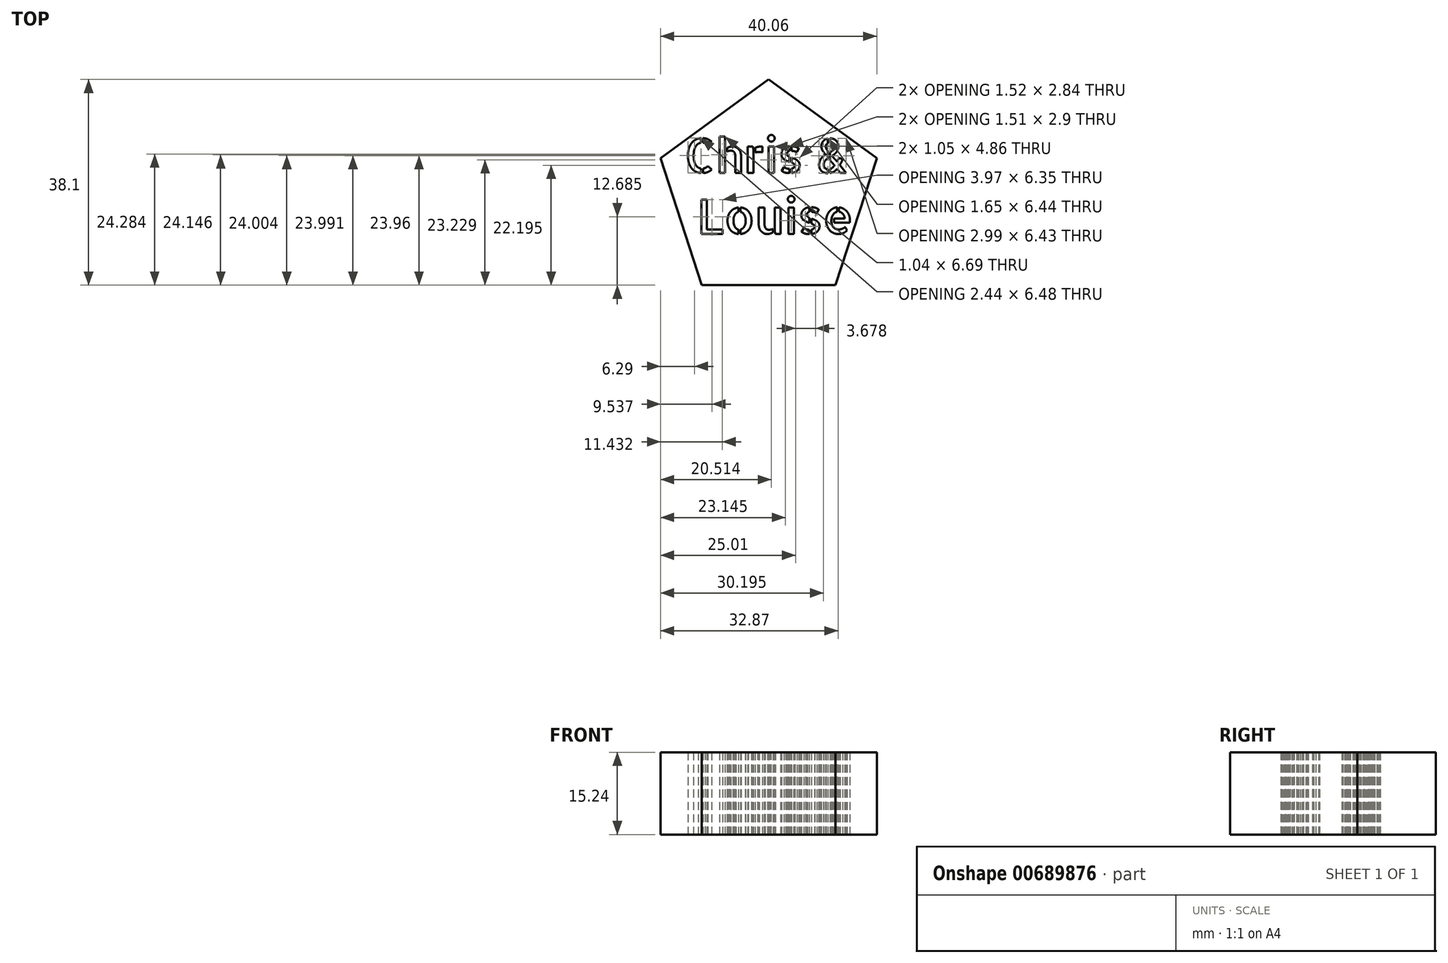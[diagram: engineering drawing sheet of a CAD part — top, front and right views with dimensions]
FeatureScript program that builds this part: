
annotation { "Feature Type Name" : "Feature", "Feature Type Description" : "" }
export const myFeature = defineFeature(function(context is Context, id is Id, definition is map)
    precondition{}
    {
        {
            var Q0;
            Q0=qCreatedBy(makeId("Top.planeOp"),FACE);
            var sketch = newSketch(context, id + "F0", { "sketchPlane" : qUnion([Q0])});
            skText(sketch, "E0", { "text": "Chris &\n Louise", "fontName": "AllertaStencil-Regular.ttf"});
            skCircle(sketch, "E1.cCircle", {"center": v(0, 0) * mm, "radius": 17.04 * mm, "construction": true});
            skLineSegment(sketch, "E1.0", {"start": v(12.38, -17.04) * mm, "end": v(-12.38, -17.04) * mm});
            skLineSegment(sketch, "E1.1", {"start": v(-12.38, -17.04) * mm, "end": v(-20.03, 6.5) * mm});
            skLineSegment(sketch, "E1.2", {"start": v(-20.03, 6.5) * mm, "end": v(0, 21.06) * mm});
            skLineSegment(sketch, "E1.3", {"start": v(0, 21.06) * mm, "end": v(20.03, 6.5) * mm});
            skLineSegment(sketch, "E1.4", {"start": v(20.03, 6.5) * mm, "end": v(12.38, -17.04) * mm});
            skPoint(sketch, "E1.0.midPoint", {"position": v(0, -17.04) * mm});
            const initialGuessF0  = {"E0": [-0.01564, 0.00376, 1, 0, 0.00635]};
            skSetInitialGuess(sketch, initialGuessF0);
            skSolve(sketch);
        }
        {
            var Q0;
            Q0 = qSketchRegion(id + "F0", true);
            extrude(context, id + "F1", {"entities" : qUnion([Q0]), "depth" : 15.24 * mm, "offsetDistance" : 25.4 * mm});
        }
    });
